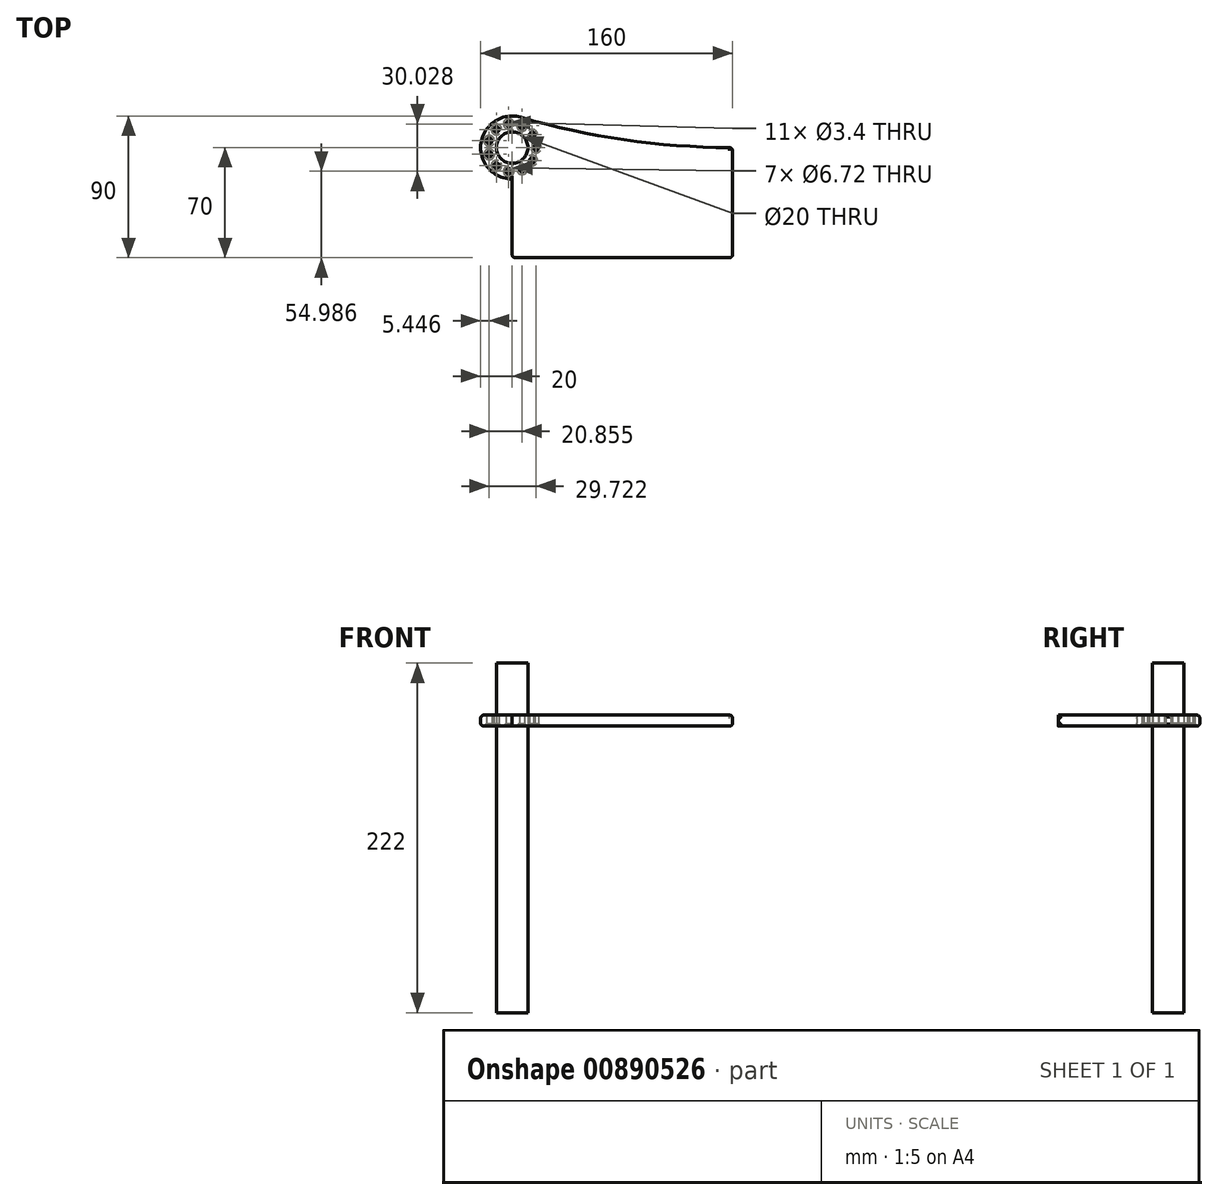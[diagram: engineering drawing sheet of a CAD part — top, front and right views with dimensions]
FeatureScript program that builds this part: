
annotation { "Feature Type Name" : "Feature", "Feature Type Description" : "" }
export const myFeature = defineFeature(function(context is Context, id is Id, definition is map)
    precondition{}
    {
        {
            var Q0;
            Q0=qCreatedBy(makeId("Top.planeOp"),FACE);
            var sketch = newSketch(context, id + "F0", { "sketchPlane" : qUnion([Q0])});
            skLineSegment(sketch, "E0.bottom", {"start": v(70, -35) * mm, "end": v(-70, -35) * mm});
            skLineSegment(sketch, "E0.top", {"start": v(70, 35) * mm, "end": v(-70, 35) * mm});
            skLineSegment(sketch, "E0.left", {"start": v(70, -35) * mm, "end": v(70, 35) * mm});
            skLineSegment(sketch, "E0.right", {"start": v(-70, -35) * mm, "end": v(-70, 35) * mm});
            skPoint(sketch, "E0.middle", {"position": v(0, 0) * mm});
            skCircle(sketch, "E1", {"center": v(-70, 35) * mm, "radius": 20 * mm});
            skArc(sketch, "E2", {"start": v(-64.4, 54.2) * mm, "mid": v(2.12, 39.82) * mm, "end": v(70, 35) * mm});
            skCircle(sketch, "E3", {"center": v(-70, 35) * mm, "radius": 10 * mm});
            skSolve(sketch);
        }
        {
            var Q0;
            Q0=makeQuery(id+"F0.imprint","IMPRINT",FACE,{"disambiguationData":[TD([[makeQuery(id+"F0.imprint","IMPRINT",EDGE,{"derivedFrom":sQuery(id+"F0.wireOp",EDGE,"E3")}),-1.0]])]});
            var Q1;
            {var subQ4=sQuery(id+"F0.wireOp",EDGE,"E0.bottom");Q1=makeQuery(id+"F0.imprint","IMPRINT",FACE,{"disambiguationData":[TD([[makeQuery(id+"F0.imprint","IMPRINT",EDGE,{"derivedFrom":subQ4}),-1.0]])]});}
            var Q2;
            {var subQ0=sQuery(id+"F0.wireOp",EDGE,"E1");var subQ4=sQuery(id+"F0.wireOp",EDGE,"E0.top");var subQ5=makeQuery(id+"F0.imprint","INTERSECT",VERTEX,{"derivedFrom":[subQ4,subQ0]});Q2=makeQuery(id+"F0.imprint","IMPRINT",FACE,{"disambiguationData":[TD([[makeQuery(id+"F0.imprint","IMPRINT",EDGE,{"disambiguationData":[TD([[subQ5,-1.0]])],"derivedFrom":subQ4}),-1.0]])]});}
            var Q3;
            {var subQ0=sQuery(id+"F0.wireOp",EDGE,"E2");Q3=makeQuery(id+"F0.imprint","IMPRINT",FACE,{"disambiguationData":[TD([[makeQuery(id+"F0.imprint","IMPRINT",EDGE,{"derivedFrom":subQ0}),-1.0]])]});}
            extrude(context, id + "F1", {"entities" : qUnion([Q0, Q1, Q2, Q3]), "depth" : 7 * mm, "offsetDistance" : 25 * mm});
        }
        {
            var Q0;
            Q0=makeQuery(id+"F1.opExtrude","CAP_EDGE",EDGE,{"disambiguationData":[OSD([sQuery(id+"F0.wireOp",EDGE,"E2")])],"isStart":false});
            var Q1;
            Q1=makeQuery(id+"F1.opExtrude","CAP_EDGE",EDGE,{"disambiguationData":[OSD([sQuery(id+"F0.wireOp",EDGE,"E0.left")])],"isStart":false});
            var Q2;
            Q2=makeQuery(id+"F1.opExtrude","CAP_EDGE",EDGE,{"disambiguationData":[OSD([sQuery(id+"F0.wireOp",EDGE,"E1")])],"isStart":false});
            var Q3;
            Q3=makeQuery(id+"F1.opExtrude","CAP_EDGE",EDGE,{"disambiguationData":[OSD([sQuery(id+"F0.wireOp",EDGE,"E0.left")])],"isStart":true});
            var Q4;
            Q4=makeQuery(id+"F1.opExtrude","CAP_EDGE",EDGE,{"disambiguationData":[OSD([sQuery(id+"F0.wireOp",EDGE,"E2")])],"isStart":true});
            var Q5;
            Q5=makeQuery(id+"F1.opExtrude","CAP_EDGE",EDGE,{"disambiguationData":[OSD([sQuery(id+"F0.wireOp",EDGE,"E1")])],"isStart":true});
            var Q6;
            Q6=makeQuery(id+"F1.opExtrude","SWEPT_EDGE",EDGE,{"disambiguationData":[OSD([sQuery(id+"F0.wireOp",EDGE,"E0.bottom"),sQuery(id+"F0.wireOp",EDGE,"E0.right")])]});
            var Q7;
            Q7=makeQuery(id+"F1.opExtrude","SWEPT_EDGE",EDGE,{"disambiguationData":[OSD([sQuery(id+"F0.wireOp",EDGE,"E0.bottom"),sQuery(id+"F0.wireOp",EDGE,"E0.left")])]});
            var Q8;
            Q8=makeQuery(id+"F1.opExtrude","SWEPT_EDGE",EDGE,{"disambiguationData":[OSD([sQuery(id+"F0.wireOp",EDGE,"E0.left"),sQuery(id+"F0.wireOp",EDGE,"E2")])]});
            fillet(context, id + "F2", {"entities" : qUnion([Q0, Q1, Q2, Q3, Q4, Q5, Q6, Q7, Q8]), "radius" : 2 * mm, "tangentPropagation" : true, "allowEdgeOverflow" : false});
        }
        {
            var Q0;
            Q0=makeQuery(id+"F0.imprint","IMPRINT",FACE,{"disambiguationData":[TD([[makeQuery(id+"F0.imprint","IMPRINT",EDGE,{"derivedFrom":sQuery(id+"F0.wireOp",EDGE,"E3")}),1.0]])]});
            extrude(context, id + "F3", {"entities" : qUnion([Q0]), "depth" : 40 * mm, "offsetDistance" : 25 * mm, "hasSecondDirection" : true, "secondDirectionOppositeDirection" : true, "secondDirectionDepth" : 182 * mm});
        }
        {
            var Q0;
            Q0=qCreatedBy(makeId("Top.planeOp"),FACE);
            var sketch = newSketch(context, id + "F4", { "sketchPlane" : qUnion([Q0])});
            skLineSegment(sketch, "E4.0", {"start": v(70, 35) * mm, "end": v(-70, 35) * mm});
            skPoint(sketch, "E5", {"position": v(-54.83, 35) * mm});
            skLineSegment(sketch, "E6.0", {"start": v(-70, -35) * mm, "end": v(-70, 35) * mm});
            skPoint(sketch, "E7.1.0", {"position": v(-57.24, 43.2) * mm});
            skPoint(sketch, "E7.2.0", {"position": v(-63.7, 48.8) * mm});
            skPoint(sketch, "E7.3.0", {"position": v(-72.16, 50.01) * mm});
            skPoint(sketch, "E7.4.0", {"position": v(-79.93, 46.46) * mm});
            skPoint(sketch, "E7.5.0", {"position": v(-84.55, 39.27) * mm});
            skPoint(sketch, "E7.6.0", {"position": v(-84.55, 30.73) * mm});
            skPoint(sketch, "E7.7.0", {"position": v(-79.93, 23.54) * mm});
            skPoint(sketch, "E7.8.0", {"position": v(-72.16, 19.99) * mm});
            skPoint(sketch, "E7.9.0", {"position": v(-63.7, 21.2) * mm});
            skPoint(sketch, "E7.10.0", {"position": v(-57.24, 26.8) * mm});
            skPoint(sketch, "E7.center", {"position": v(-70, 35) * mm});
            skSolve(sketch);
        }
        {
            var Q0;
            Q0=sQuery(id+"F4.wireOp",VERTEX,"E7.2.0");
            var Q1;
            Q1=sQuery(id+"F4.wireOp",VERTEX,"E7.1.0");
            var Q2;
            Q2=sQuery(id+"F4.wireOp",VERTEX,"E5");
            var Q3;
            Q3=sQuery(id+"F4.wireOp",VERTEX,"E7.10.0");
            var Q4;
            Q4=sQuery(id+"F4.wireOp",VERTEX,"E7.9.0");
            var Q5;
            Q5=sQuery(id+"F4.wireOp",VERTEX,"E7.8.0");
            var Q6;
            Q6=sQuery(id+"F4.wireOp",VERTEX,"E7.7.0");
            var Q7;
            Q7=sQuery(id+"F4.wireOp",VERTEX,"E7.6.0");
            var Q8;
            Q8=sQuery(id+"F4.wireOp",VERTEX,"E7.5.0");
            var Q9;
            Q9=sQuery(id+"F4.wireOp",VERTEX,"E7.4.0");
            var Q10;
            Q10=sQuery(id+"F4.wireOp",VERTEX,"E7.3.0");
            var Q11;
            Q11=makeQuery(id+"F1.opExtrude","SWEPT_BODY",BODY,{"disambiguationData":[OSD([sQuery(id+"F0.wireOp",EDGE,"E0.bottom"),sQuery(id+"F0.wireOp",EDGE,"E0.left"),sQuery(id+"F0.wireOp",EDGE,"E0.right"),sQuery(id+"F0.wireOp",EDGE,"E1"),sQuery(id+"F0.wireOp",EDGE,"E2"),sQuery(id+"F0.wireOp",EDGE,"E3")])]});
            hole(context, id + "F5", {"style" : HoleStyle.C_SINK, "endStyle" : HoleEndStyle.THROUGH, "oppositeDirection" : true, "standardTappedOrClearance" : lookupTablePath({ "fit" : "Normal", "standard" : "ISO", "size" : "M3", "type" : "Clearance" }), "standardBlindInLast" : lookupTablePath({ "fit" : "Normal", "standard" : "ISO", "size" : "M3", "type" : "Clearance" }), "holeDiameter" : 3.4 * mm, "cSinkDiameter" : 6.72 * mm, "cSinkAngle" : 90 * degree, "majorDiameter" : 5 * mm, "isTappedThrough" : true, "tappedDepth" : 12 * mm, "tapClearance" : 3, "locations" : qUnion([Q0, Q1, Q2, Q3, Q4, Q5, Q6, Q7, Q8, Q9, Q10]), "scope" : qUnion([Q11])});
        }
    });
